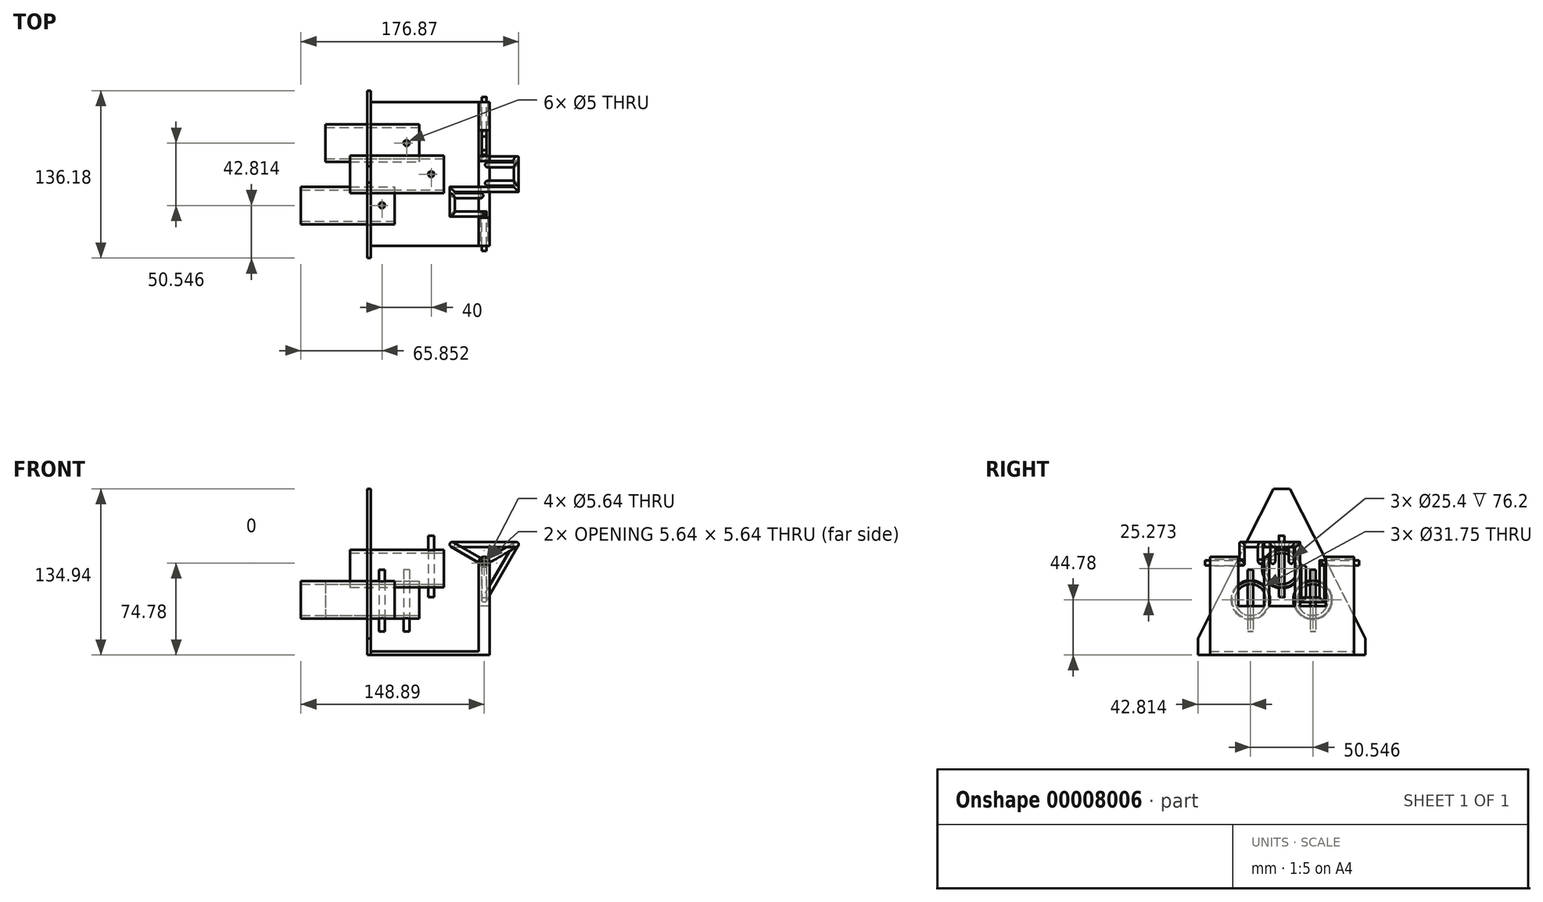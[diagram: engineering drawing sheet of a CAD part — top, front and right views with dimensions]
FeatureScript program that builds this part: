
annotation { "Feature Type Name" : "Feature", "Feature Type Description" : "" }
export const myFeature = defineFeature(function(context is Context, id is Id, definition is map)
    precondition{}
    {
        {
            var Q0;
            Q0=qCreatedBy(makeId("Front.planeOp"),FACE);
            var sketch = newSketch(context, id + "F0", { "sketchPlane" : qUnion([Q0])});
            skCircle(sketch, "E0", {"center": v(0, 0) * mm, "radius": 2 * mm});
            skLineSegment(sketch, "E1", {"start": v(0, 0) * mm, "end": v(-25.98, 15) * mm, "construction": true});
            skLineSegment(sketch, "E2", {"start": v(0, 0) * mm, "end": v(25.98, 15) * mm, "construction": true});
            skLineSegment(sketch, "E3", {"start": v(0, 0) * mm, "end": v(0, -30) * mm, "construction": true});
            skSolve(sketch);
        }
        {
            var Q0;
            Q0=qCreatedBy(makeId("Top.planeOp"),FACE);
            var sketch = newSketch(context, id + "F1", { "sketchPlane" : qUnion([Q0])});
            skLineSegment(sketch, "E4", {"start": v(0, 0) * mm, "end": v(0, 30) * mm});
            skLineSegment(sketch, "E5", {"start": v(0, 45) * mm, "end": v(0, 55) * mm});
            skLineSegment(sketch, "E6", {"start": v(0, 70) * mm, "end": v(0, 80) * mm});
            skLineSegment(sketch, "E7", {"start": v(0, 95) * mm, "end": v(0, 125) * mm});
            skLineSegment(sketch, "E8", {"start": v(0, 30) * mm, "end": v(0, 45) * mm, "construction": true});
            skLineSegment(sketch, "E9", {"start": v(0, 55) * mm, "end": v(0, 70) * mm, "construction": true});
            skLineSegment(sketch, "E10", {"start": v(0, 80) * mm, "end": v(0, 95) * mm, "construction": true});
            skSolve(sketch);
        }
        {
            var Q0;
            Q0=sQuery(id+"F0.wireOp",VERTEX,"E1.end");
            var Q1;
            Q1=sQuery(id+"F0.wireOp",VERTEX,"E2.start");
            var Q2;
            Q2=sQuery(id+"F1.wireOp",VERTEX,"E8.start");
            cPlane(context, id + "F2", {"entities" : qUnion([Q0, Q1, Q2]), "cplaneType" : CPlaneType.THREE_POINT, "offset" : 150 * mm, "width" : 150 * mm, "height" : 150 * mm});
        }
        {
            var Q0;
            Q0=sQuery(id+"F0.wireOp",VERTEX,"E2.end");
            var Q1;
            Q1=sQuery(id+"F0.wireOp",VERTEX,"E2.start");
            var Q2;
            Q2=sQuery(id+"F1.wireOp",VERTEX,"E8.start");
            cPlane(context, id + "F3", {"entities" : qUnion([Q0, Q1, Q2]), "cplaneType" : CPlaneType.THREE_POINT, "offset" : 150 * mm, "width" : 150 * mm, "height" : 150 * mm});
        }
        {
            var Q0;
            Q0=qCreatedBy(id+"F2.planeOp",FACE);
            var sketch = newSketch(context, id + "F4", { "sketchPlane" : qUnion([Q0])});
            skLineSegment(sketch, "E11.0", {"start": v(0, 0) * mm, "end": v(-30, 0) * mm, "construction": true});
            skLineSegment(sketch, "E12.0", {"start": v(0, -30) * mm, "end": v(0, -45) * mm, "construction": true});
            skLineSegment(sketch, "E13", {"start": v(0, -30) * mm, "end": v(-30, -30) * mm});
            skLineSegment(sketch, "E14", {"start": v(-30, -30) * mm, "end": v(-30, -45) * mm});
            skLineSegment(sketch, "E15", {"start": v(-30, -45) * mm, "end": v(0, -45) * mm});
            skSolve(sketch);
        }
        {
            var Q0;
            Q0=qCreatedBy(id+"F3.planeOp",FACE);
            var sketch = newSketch(context, id + "F5", { "sketchPlane" : qUnion([Q0])});
            skLineSegment(sketch, "E16.0", {"start": v(0, 0) * mm, "end": v(30, 0) * mm, "construction": true});
            skLineSegment(sketch, "E16.1", {"start": v(0, 55) * mm, "end": v(0, 70) * mm, "construction": true});
            skLineSegment(sketch, "E17", {"start": v(0, 55) * mm, "end": v(30, 55) * mm});
            skLineSegment(sketch, "E18", {"start": v(30, 55) * mm, "end": v(30, 70) * mm});
            skLineSegment(sketch, "E19", {"start": v(30, 70) * mm, "end": v(0, 70) * mm});
            skSolve(sketch);
        }
        {
            var Q0;
            Q0=qCreatedBy(makeId("Right.planeOp"),FACE);
            var sketch = newSketch(context, id + "F6", { "sketchPlane" : qUnion([Q0])});
            skLineSegment(sketch, "E20.0", {"start": v(0, 0) * mm, "end": v(0, -30) * mm, "construction": true});
            skLineSegment(sketch, "E20.1", {"start": v(80, 0) * mm, "end": v(95, 0) * mm, "construction": true});
            skLineSegment(sketch, "E21", {"start": v(80, 0) * mm, "end": v(80, -30) * mm});
            skLineSegment(sketch, "E22", {"start": v(80, -30) * mm, "end": v(95, -30) * mm});
            skLineSegment(sketch, "E23", {"start": v(95, -30) * mm, "end": v(95, 0) * mm});
            skSolve(sketch);
        }
        {
            var Q0;
            Q0=makeQuery(id+"F0.imprint","IMPRINT",FACE,{"disambiguationData":[TD([[makeQuery(id+"F0.imprint","IMPRINT",EDGE,{"derivedFrom":sQuery(id+"F0.wireOp",EDGE,"E0")}),1.0]])]});
            var Q1;
            Q1=sQuery(id+"F1.wireOp",EDGE,"E4");
            var Q2;
            Q2=sQuery(id+"F4.wireOp",EDGE,"E13");
            var Q3;
            Q3=sQuery(id+"F4.wireOp",EDGE,"E14");
            var Q4;
            Q4=sQuery(id+"F4.wireOp",EDGE,"E15");
            var Q5;
            Q5=sQuery(id+"F1.wireOp",EDGE,"E5");
            var Q6;
            Q6=sQuery(id+"F5.wireOp",EDGE,"E17");
            var Q7;
            Q7=sQuery(id+"F5.wireOp",EDGE,"E19");
            var Q8;
            Q8=sQuery(id+"F5.wireOp",EDGE,"E18");
            var Q9;
            Q9=sQuery(id+"F1.wireOp",EDGE,"E6");
            var Q10;
            Q10=sQuery(id+"F6.wireOp",EDGE,"E21");
            var Q11;
            Q11=sQuery(id+"F6.wireOp",EDGE,"E22");
            var Q12;
            Q12=sQuery(id+"F6.wireOp",EDGE,"E23");
            var Q13;
            Q13=sQuery(id+"F1.wireOp",EDGE,"E7");
            sweep(context, id + "F7", {"profiles" : qUnion([Q0]), "path" : qUnion([Q1, Q2, Q3, Q4, Q5, Q6, Q7, Q8, Q9, Q10, Q11, Q12, Q13])});
        }
        {
            var Q0;
            Q0=qCreatedBy(makeId("Right.planeOp"),FACE);
            var sketch = newSketch(context, id + "F8", { "sketchPlane" : qUnion([Q0])});
            skLineSegment(sketch, "E24", {"start": v(4, -44.64) * mm, "end": v(4, 5) * mm});
            skLineSegment(sketch, "E25", {"start": v(4, 5) * mm, "end": v(27, 5) * mm});
            skLineSegment(sketch, "E26", {"start": v(27, 5) * mm, "end": v(27, -35) * mm});
            skLineSegment(sketch, "E27", {"start": v(27, -35) * mm, "end": v(47.92, -35) * mm});
            skLineSegment(sketch, "E28", {"start": v(47.92, -35) * mm, "end": v(47.92, 5) * mm});
            skLineSegment(sketch, "E29", {"start": v(47.92, 5) * mm, "end": v(52.04, 5) * mm});
            skLineSegment(sketch, "E30", {"start": v(52.04, 5) * mm, "end": v(52.04, -35) * mm});
            skLineSegment(sketch, "E31", {"start": v(52.04, -35) * mm, "end": v(72.96, -35) * mm});
            skLineSegment(sketch, "E32", {"start": v(72.96, -35) * mm, "end": v(72.96, 5) * mm});
            skLineSegment(sketch, "E33", {"start": v(72.96, 5) * mm, "end": v(77.08, 5) * mm});
            skLineSegment(sketch, "E34", {"start": v(77.08, 5) * mm, "end": v(77.08, -35) * mm});
            skLineSegment(sketch, "E35", {"start": v(77.08, -35) * mm, "end": v(98, -35) * mm});
            skLineSegment(sketch, "E36", {"start": v(98, -35) * mm, "end": v(98, 5) * mm});
            skLineSegment(sketch, "E37", {"start": v(98, 5) * mm, "end": v(121, 5) * mm});
            skLineSegment(sketch, "E38", {"start": v(121, 5) * mm, "end": v(121, -44.64) * mm});
            skLineSegment(sketch, "E39", {"start": v(121, -44.64) * mm, "end": v(4, -44.64) * mm});
            skSolve(sketch);
        }
        {
            var Q0;
            Q0=makeQuery(id+"F8.imprint","IMPRINT",FACE,{"disambiguationData":[TD([[makeQuery(id+"F8.imprint","IMPRINT",EDGE,{"derivedFrom":sQuery(id+"F8.wireOp",EDGE,"E24")}),-1.0]])]});
            extrude(context, id + "F9", {"entities" : qUnion([Q0]), "endBound" : BoundingType.SYMMETRIC, "depth" : 9 * mm});
        }
        {
            var Q0;
            Q0=makeQuery(id+"F9.opExtrude","SWEPT_FACE",FACE,{"disambiguationData":[OSD([sQuery(id+"F8.wireOp",EDGE,"E24")])]});
            var sketch = newSketch(context, id + "F10", { "sketchPlane" : qUnion([Q0])});
            skCircle(sketch, "E40", {"center": v(0, 0) * mm, "radius": 2.82 * mm});
            skSolve(sketch);
        }
        {
            var Q0;
            Q0=makeQuery(id+"F9.opExtrude","CAP_FACE",FACE,{"disambiguationData":[OSD([sQuery(id+"F8.wireOp",EDGE,"E24"),sQuery(id+"F8.wireOp",EDGE,"E25"),sQuery(id+"F8.wireOp",EDGE,"E26"),sQuery(id+"F8.wireOp",EDGE,"E27"),sQuery(id+"F8.wireOp",EDGE,"E28"),sQuery(id+"F8.wireOp",EDGE,"E29"),sQuery(id+"F8.wireOp",EDGE,"E30"),sQuery(id+"F8.wireOp",EDGE,"E31"),sQuery(id+"F8.wireOp",EDGE,"E32"),sQuery(id+"F8.wireOp",EDGE,"E33"),sQuery(id+"F8.wireOp",EDGE,"E34"),sQuery(id+"F8.wireOp",EDGE,"E35"),sQuery(id+"F8.wireOp",EDGE,"E36"),sQuery(id+"F8.wireOp",EDGE,"E37"),sQuery(id+"F8.wireOp",EDGE,"E38"),sQuery(id+"F8.wireOp",EDGE,"E39")])],"isStart":false});
            var sketch = newSketch(context, id + "F11", { "sketchPlane" : qUnion([Q0])});
            skLineSegment(sketch, "E41.0.0", {"start": v(4, 5) * mm, "end": v(4, -44.64) * mm});
            skLineSegment(sketch, "E41.0.1", {"start": v(4, -44.64) * mm, "end": v(121, -44.64) * mm});
            skLineSegment(sketch, "E41.0.2", {"start": v(121, -44.64) * mm, "end": v(121, 5) * mm});
            skLineSegment(sketch, "E41.0.3", {"start": v(121, 5) * mm, "end": v(98, 5) * mm});
            skLineSegment(sketch, "E41.0.4", {"start": v(98, 5) * mm, "end": v(98, -35) * mm});
            skLineSegment(sketch, "E41.0.5", {"start": v(98, -35) * mm, "end": v(77.08, -35) * mm});
            skLineSegment(sketch, "E41.0.6", {"start": v(77.08, -35) * mm, "end": v(77.08, 5) * mm});
            skLineSegment(sketch, "E41.0.7", {"start": v(77.08, 5) * mm, "end": v(72.96, 5) * mm});
            skLineSegment(sketch, "E41.0.8", {"start": v(72.96, 5) * mm, "end": v(72.96, -35) * mm});
            skLineSegment(sketch, "E41.0.9", {"start": v(72.96, -35) * mm, "end": v(52.04, -35) * mm});
            skLineSegment(sketch, "E41.0.10", {"start": v(52.04, -35) * mm, "end": v(52.04, 5) * mm});
            skLineSegment(sketch, "E41.0.11", {"start": v(52.04, 5) * mm, "end": v(47.92, 5) * mm});
            skLineSegment(sketch, "E41.0.12", {"start": v(47.92, 5) * mm, "end": v(47.92, -35) * mm});
            skLineSegment(sketch, "E41.0.13", {"start": v(47.92, -35) * mm, "end": v(27, -35) * mm});
            skLineSegment(sketch, "E41.0.14", {"start": v(27, -35) * mm, "end": v(27, 5) * mm});
            skLineSegment(sketch, "E41.0.15", {"start": v(27, 5) * mm, "end": v(4, 5) * mm});
            skLineSegment(sketch, "E42", {"start": v(47.92, -35) * mm, "end": v(52.04, -35) * mm});
            skLineSegment(sketch, "E43", {"start": v(72.96, -35) * mm, "end": v(77.08, -35) * mm});
            skSolve(sketch);
        }
        {
            var Q0;
            Q0=makeQuery(id+"F11.imprint","IMPRINT",FACE,{"disambiguationData":[TD([[makeQuery(id+"F11.imprint","IMPRINT",EDGE,{"derivedFrom":sQuery(id+"F11.wireOp",EDGE,"E41.0.0")}),-1.0]])]});
            extrude(context, id + "F12", {"entities" : qUnion([Q0]), "oppositeDirection" : true, "depth" : 9 * mm});
        }
        {
            var Q0;
            Q0=makeQuery(id+"F10.imprint","IMPRINT",FACE,{"disambiguationData":[TD([[makeQuery(id+"F10.imprint","IMPRINT",EDGE,{"derivedFrom":sQuery(id+"F10.wireOp",EDGE,"E40")}),1.0]])]});
            extrude(context, id + "F13", {"entities" : qUnion([Q0]), "operationType" : NewBodyOperationType.REMOVE, "endBound" : BoundingType.THROUGH_ALL, "oppositeDirection" : true, "depth" : 25 * mm});
        }
        {
            var Q0;
            Q0=makeQuery(id+"F9.opExtrude","CAP_EDGE",EDGE,{"disambiguationData":[OSD([sQuery(id+"F8.wireOp",EDGE,"E25")])],"isStart":true});
            var Q1;
            Q1=makeQuery(id+"F9.opExtrude","CAP_EDGE",EDGE,{"disambiguationData":[OSD([sQuery(id+"F8.wireOp",EDGE,"E29")])],"isStart":false});
            var Q2;
            Q2=makeQuery(id+"F9.opExtrude","CAP_EDGE",EDGE,{"disambiguationData":[OSD([sQuery(id+"F8.wireOp",EDGE,"E29")])],"isStart":true});
            var Q3;
            Q3=makeQuery(id+"F9.opExtrude","CAP_EDGE",EDGE,{"disambiguationData":[OSD([sQuery(id+"F8.wireOp",EDGE,"E33")])],"isStart":false});
            var Q4;
            Q4=makeQuery(id+"F9.opExtrude","CAP_EDGE",EDGE,{"disambiguationData":[OSD([sQuery(id+"F8.wireOp",EDGE,"E33")])],"isStart":true});
            var Q5;
            Q5=makeQuery(id+"F9.opExtrude","CAP_EDGE",EDGE,{"disambiguationData":[OSD([sQuery(id+"F8.wireOp",EDGE,"E37")])],"isStart":false});
            var Q6;
            Q6=makeQuery(id+"F9.opExtrude","CAP_EDGE",EDGE,{"disambiguationData":[OSD([sQuery(id+"F8.wireOp",EDGE,"E37")])],"isStart":true});
            var Q7;
            Q7=makeQuery(id+"F9.opExtrude","CAP_EDGE",EDGE,{"disambiguationData":[OSD([sQuery(id+"F8.wireOp",EDGE,"E25")])],"isStart":false});
            var Q8;
            Q8=makeQuery(id+"F12.opExtrude","CAP_EDGE",EDGE,{"disambiguationData":[OSD([sQuery(id+"F11.wireOp",EDGE,"E41.0.15")])],"isStart":true});
            var Q9;
            Q9=makeQuery(id+"F12.opExtrude","CAP_EDGE",EDGE,{"disambiguationData":[OSD([sQuery(id+"F11.wireOp",EDGE,"E41.0.15")])],"isStart":false});
            var Q10;
            Q10=makeQuery(id+"F12.opExtrude","CAP_EDGE",EDGE,{"disambiguationData":[OSD([sQuery(id+"F11.wireOp",EDGE,"E41.0.3")])],"isStart":true});
            var Q11;
            Q11=makeQuery(id+"F12.opExtrude","CAP_EDGE",EDGE,{"disambiguationData":[OSD([sQuery(id+"F11.wireOp",EDGE,"E41.0.3")])],"isStart":false});
            fillet(context, id + "F14", {"entities" : qUnion([Q0, Q1, Q2, Q3, Q4, Q5, Q6, Q7, Q8, Q9, Q10, Q11]), "radius" : 4.5 * mm, "tangentPropagation" : true, "allowEdgeOverflow" : false});
        }
        {
            var Q0;
            Q0=qCreatedBy(id+"F2.planeOp",FACE);
            var sketch = newSketch(context, id + "F15", { "sketchPlane" : qUnion([Q0])});
            skLineSegment(sketch, "E44.0", {"start": v(0, -45) * mm, "end": v(0, -55) * mm, "construction": true});
            skLineSegment(sketch, "E44.1", {"start": v(0, 0) * mm, "end": v(-30, 0) * mm, "construction": true});
            skLineSegment(sketch, "E45.0", {"start": v(0, -30) * mm, "end": v(0, -45) * mm, "construction": true});
            skLineSegment(sketch, "E46", {"start": v(0, -30) * mm, "end": v(-30, -30) * mm});
            skLineSegment(sketch, "E47", {"start": v(0, -50) * mm, "end": v(-30, -50) * mm, "construction": true});
            skLineSegment(sketch, "E48", {"start": v(-30, -50) * mm, "end": v(-30, -30) * mm});
            skSolve(sketch);
        }
        {
            var Q0;
            Q0=qCreatedBy(id+"F3.planeOp",FACE);
            var sketch = newSketch(context, id + "F16", { "sketchPlane" : qUnion([Q0])});
            skLineSegment(sketch, "E49.0", {"start": v(0, 0) * mm, "end": v(30, 0) * mm, "construction": true});
            skPoint(sketch, "E49.1", {"position": v(0, 50) * mm});
            skLineSegment(sketch, "E49.2", {"start": v(0, 70) * mm, "end": v(0, 80) * mm, "construction": true});
            skLineSegment(sketch, "E50", {"start": v(0, 75) * mm, "end": v(30, 75) * mm, "construction": true});
            skLineSegment(sketch, "E51", {"start": v(30, 75) * mm, "end": v(30, 50) * mm});
            skSolve(sketch);
        }
        {
            var Q0;
            Q0=sQuery(id+"F16.wireOp",VERTEX,"E50.end");
            var Q1;
            Q1=sQuery(id+"F16.wireOp",VERTEX,"E51.end");
            var Q2;
            Q2=sQuery(id+"F15.wireOp",VERTEX,"E47.end");
            cPlane(context, id + "F17", {"entities" : qUnion([Q0, Q1, Q2]), "cplaneType" : CPlaneType.THREE_POINT, "offset" : 150 * mm, "width" : 150 * mm, "height" : 150 * mm});
        }
        {
            var Q0;
            Q0=qCreatedBy(id+"F17.planeOp",FACE);
            var sketch = newSketch(context, id + "F18", { "sketchPlane" : qUnion([Q0])});
            skPoint(sketch, "E52.0", {"position": v(25.98, 50) * mm});
            skPoint(sketch, "E52.1", {"position": v(-25.98, 50) * mm});
            skLineSegment(sketch, "E53", {"start": v(-25.98, 50) * mm, "end": v(25.98, 50) * mm});
            skSolve(sketch);
        }
        {
            var Q0;
            Q0=sQuery(id+"F6.wireOp",VERTEX,"E22.end");
            var Q1;
            Q1=sQuery(id+"F6.wireOp",VERTEX,"E22.start");
            var Q2;
            Q2=sQuery(id+"F16.wireOp",VERTEX,"E51.start");
            cPlane(context, id + "F19", {"entities" : qUnion([Q0, Q1, Q2]), "cplaneType" : CPlaneType.THREE_POINT, "offset" : 150 * mm, "width" : 150 * mm, "height" : 150 * mm});
        }
        {
            var Q0;
            Q0=qCreatedBy(id+"F19.planeOp",FACE);
            var sketch = newSketch(context, id + "F20", { "sketchPlane" : qUnion([Q0])});
            skPoint(sketch, "E54.0", {"position": v(95, -25.98) * mm});
            skPoint(sketch, "E54.1", {"position": v(75, 25.98) * mm});
            skLineSegment(sketch, "E55", {"start": v(75, 25.98) * mm, "end": v(75, -25.98) * mm});
            skLineSegment(sketch, "E56", {"start": v(75, -25.98) * mm, "end": v(95, -25.98) * mm});
            skSolve(sketch);
        }
        {
            var Q0;
            Q0=makeQuery(id+"F0.imprint","IMPRINT",FACE,{"disambiguationData":[TD([[makeQuery(id+"F0.imprint","IMPRINT",EDGE,{"derivedFrom":sQuery(id+"F0.wireOp",EDGE,"E0")}),1.0]])]});
            var Q1;
            Q1=sQuery(id+"F1.wireOp",EDGE,"E4");
            var Q2;
            Q2=sQuery(id+"F15.wireOp",EDGE,"E46");
            var Q3;
            Q3=sQuery(id+"F15.wireOp",EDGE,"E48");
            var Q4;
            Q4=sQuery(id+"F18.wireOp",EDGE,"E53");
            var Q5;
            Q5=sQuery(id+"F16.wireOp",EDGE,"E51");
            var Q6;
            Q6=sQuery(id+"F20.wireOp",EDGE,"E55");
            var Q7;
            Q7=sQuery(id+"F20.wireOp",EDGE,"E56");
            var Q8;
            Q8=sQuery(id+"F6.wireOp",EDGE,"E23");
            var Q9;
            Q9=sQuery(id+"F1.wireOp",EDGE,"E7");
            sweep(context, id + "F21", {"profiles" : qUnion([Q0]), "path" : qUnion([Q1, Q2, Q3, Q4, Q5, Q6, Q7, Q8, Q9])});
        }
        {
            var Q0;
            Q0=makeQuery(id+"F12.opExtrude","CAP_FACE",FACE,{"disambiguationData":[OSD([sQuery(id+"F11.wireOp",EDGE,"E41.0.0"),sQuery(id+"F11.wireOp",EDGE,"E41.0.1"),sQuery(id+"F11.wireOp",EDGE,"E41.0.2"),sQuery(id+"F11.wireOp",EDGE,"E41.0.3"),sQuery(id+"F11.wireOp",EDGE,"E41.0.4"),sQuery(id+"F11.wireOp",EDGE,"E41.0.5"),sQuery(id+"F11.wireOp",EDGE,"E41.0.9"),sQuery(id+"F11.wireOp",EDGE,"E41.0.13"),sQuery(id+"F11.wireOp",EDGE,"E41.0.14"),sQuery(id+"F11.wireOp",EDGE,"E41.0.15"),sQuery(id+"F11.wireOp",EDGE,"E42"),sQuery(id+"F11.wireOp",EDGE,"E43")])],"isStart":false});
            var sketch = newSketch(context, id + "F22", { "sketchPlane" : qUnion([Q0])});
            skCircle(sketch, "E57", {"center": v(-87.5, -30) * mm, "radius": 15.24 * mm});
            skCircle(sketch, "E58", {"center": v(-36.95, -30) * mm, "radius": 15.24 * mm});
            skCircle(sketch, "E59", {"center": v(-62.23, -4.73) * mm, "radius": 15.24 * mm});
            skLineSegment(sketch, "E60", {"start": v(-62.23, -30) * mm, "end": v(-62.23, -4.73) * mm, "construction": true});
            skLineSegment(sketch, "E61", {"start": v(-87.5, -30) * mm, "end": v(-62.23, -30) * mm, "construction": true});
            skLineSegment(sketch, "E62", {"start": v(-62.23, -30) * mm, "end": v(-36.95, -30) * mm, "construction": true});
            skCircle(sketch, "E63", {"center": v(-87.5, -30) * mm, "radius": 12.7 * mm});
            skCircle(sketch, "E64", {"center": v(-62.23, -4.73) * mm, "radius": 12.7 * mm});
            skCircle(sketch, "E65", {"center": v(-36.95, -30) * mm, "radius": 12.7 * mm});
            skSolve(sketch);
        }
        {
            var Q0;
            {var subQ3=sQuery(id+"F22.wireOp",EDGE,"E57");var subQ5=makeQuery(id+"F12.opExtrude","CAP_EDGE",EDGE,{"disambiguationData":[OSD([sQuery(id+"F11.wireOp",EDGE,"E41.0.4")])],"isStart":false});var subQ7=makeQuery(id+"F22.imprint","INTERSECT",VERTEX,{"derivedFrom":[subQ5,subQ3]});Q0=makeQuery(id+"F22.imprint","IMPRINT",FACE,{"disambiguationData":[TD([[makeQuery(id+"F22.imprint","IMPRINT",EDGE,{"disambiguationData":[TD([[subQ7,1.0]])],"derivedFrom":subQ5}),-1.0]])]});}
            var Q1;
            {var subQ3=sQuery(id+"F22.wireOp",EDGE,"E57");var subQ5=makeQuery(id+"F12.opExtrude","CAP_EDGE",EDGE,{"disambiguationData":[OSD([sQuery(id+"F11.wireOp",EDGE,"E41.0.1")])],"isStart":false});var subQ7=makeQuery(id+"F22.imprint","INTERSECT",VERTEX,{"disambiguationData":[OD(0.0)],"derivedFrom":[subQ5,subQ3]});Q1=makeQuery(id+"F22.imprint","IMPRINT",FACE,{"disambiguationData":[TD([[makeQuery(id+"F22.imprint","IMPRINT",EDGE,{"disambiguationData":[TD([[subQ7,1.0]])],"derivedFrom":subQ3}),1.0]])]});}
            var Q2;
            Q2=makeQuery(id+"F22.imprint","IMPRINT",FACE,{"disambiguationData":[TD([[makeQuery(id+"F22.imprint","IMPRINT",EDGE,{"derivedFrom":sQuery(id+"F22.wireOp",EDGE,"E59")}),1.0]])]});
            var Q3;
            {var subQ3=sQuery(id+"F22.wireOp",EDGE,"E58");var subQ5=makeQuery(id+"F12.opExtrude","CAP_EDGE",EDGE,{"disambiguationData":[OSD([sQuery(id+"F11.wireOp",EDGE,"E41.0.14")])],"isStart":false});var subQ7=makeQuery(id+"F22.imprint","INTERSECT",VERTEX,{"derivedFrom":[subQ5,subQ3]});Q3=makeQuery(id+"F22.imprint","IMPRINT",FACE,{"disambiguationData":[TD([[makeQuery(id+"F22.imprint","IMPRINT",EDGE,{"disambiguationData":[TD([[subQ7,-1.0]])],"derivedFrom":subQ5}),-1.0]])]});}
            var Q4;
            {var subQ3=sQuery(id+"F22.wireOp",EDGE,"E58");var subQ8=makeQuery(id+"F12.opExtrude","CAP_EDGE",EDGE,{"disambiguationData":[OSD([sQuery(id+"F11.wireOp",EDGE,"E41.0.14")])],"isStart":false});var subQ10=makeQuery(id+"F22.imprint","INTERSECT",VERTEX,{"derivedFrom":[subQ8,subQ3]});Q4=makeQuery(id+"F22.imprint","IMPRINT",FACE,{"disambiguationData":[TD([[makeQuery(id+"F22.imprint","IMPRINT",EDGE,{"disambiguationData":[TD([[subQ10,1.0]])],"derivedFrom":subQ3}),1.0]])]});}
            var Q5;
            {var subQ0=makeQuery(id+"F12.opExtrude","CAP_EDGE",EDGE,{"disambiguationData":[OSD([sQuery(id+"F11.wireOp",EDGE,"E41.0.1")])],"isStart":false});var subQ1=sQuery(id+"F22.wireOp",EDGE,"E57");var subQ3=makeQuery(id+"F22.imprint","INTERSECT",VERTEX,{"disambiguationData":[OD(0.0)],"derivedFrom":[subQ0,subQ1]});Q5=makeQuery(id+"F22.imprint","IMPRINT",FACE,{"disambiguationData":[TD([[makeQuery(id+"F22.imprint","IMPRINT",EDGE,{"disambiguationData":[TD([[subQ3,-1.0]])],"derivedFrom":subQ1}),1.0]])]});}
            var Q6;
            {var subQ0=makeQuery(id+"F12.opExtrude","CAP_EDGE",EDGE,{"disambiguationData":[OSD([sQuery(id+"F11.wireOp",EDGE,"E41.0.1")])],"isStart":false});var subQ1=sQuery(id+"F22.wireOp",EDGE,"E58");var subQ3=makeQuery(id+"F22.imprint","INTERSECT",VERTEX,{"disambiguationData":[OD(0.0)],"derivedFrom":[subQ0,subQ1]});Q6=makeQuery(id+"F22.imprint","IMPRINT",FACE,{"disambiguationData":[TD([[makeQuery(id+"F22.imprint","IMPRINT",EDGE,{"disambiguationData":[TD([[subQ3,-1.0]])],"derivedFrom":subQ1}),1.0]])]});}
            extrude(context, id + "F23", {"entities" : qUnion([Q0, Q1, Q2, Q3, Q4, Q5, Q6]), "depth" : 76.2 * mm});
        }
        {
            var Q0;
            Q0=makeQuery(id+"F23.opExtrude","SWEPT_BODY",BODY,{"disambiguationData":[OSD([sQuery(id+"F22.wireOp",EDGE,"E59"),sQuery(id+"F22.wireOp",EDGE,"E64")])]});
            var Q1;
            Q1=makeQuery(id+"F23.opExtrude","SWEPT_BODY",BODY,{"disambiguationData":[OSD([sQuery(id+"F11.wireOp",EDGE,"E41.0.1"),sQuery(id+"F22.wireOp",EDGE,"E57"),sQuery(id+"F22.wireOp",EDGE,"E63")])]});
            var Q2;
            Q2=makeQuery(id+"F23.opExtrude","SWEPT_BODY",BODY,{"disambiguationData":[OSD([sQuery(id+"F11.wireOp",EDGE,"E41.0.1"),sQuery(id+"F22.wireOp",EDGE,"E58"),sQuery(id+"F22.wireOp",EDGE,"E65")])]});
            transform(context, id + "F24", {"entities" : qUnion([Q0, Q1, Q2]), "transformType" : TransformType.TRANSLATION_3D, "dx" : -48.19 * mm, "dy" : 0 * mm, "dz" : 0 * mm, "makeCopy" : false});
        }
        {
            var Q0;
            Q0=makeQuery(id+"F9.opExtrude","SWEPT_FACE",FACE,{"disambiguationData":[OSD([sQuery(id+"F8.wireOp",EDGE,"E31")])]});
            var sketch = newSketch(context, id + "F25", { "sketchPlane" : qUnion([Q0])});
            skCircle(sketch, "E66", {"center": v(-63.04, 87.5) * mm, "radius": 2.5 * mm});
            skCircle(sketch, "E67", {"center": v(-63.04, 62.23) * mm, "radius": 2.5 * mm});
            skCircle(sketch, "E68", {"center": v(-63.04, 36.95) * mm, "radius": 2.5 * mm});
            skLineSegment(sketch, "E69", {"start": v(-63.04, 87.5) * mm, "end": v(-63.04, 62.23) * mm, "construction": true});
            skLineSegment(sketch, "E70", {"start": v(-63.04, 62.23) * mm, "end": v(-63.04, 36.95) * mm, "construction": true});
            skLineSegment(sketch, "E71", {"start": v(-128.81, 36.95) * mm, "end": v(-63.04, 36.95) * mm, "construction": true});
            skLineSegment(sketch, "E72.0", {"start": v(-128.89, 46.99) * mm, "end": v(-128.89, 77.47) * mm});
            skLineSegment(sketch, "E73", {"start": v(-128.89, 62.23) * mm, "end": v(-63.04, 62.23) * mm, "construction": true});
            skLineSegment(sketch, "E74.0", {"start": v(-128.89, 72.26) * mm, "end": v(-128.89, 102.74) * mm});
            skLineSegment(sketch, "E75", {"start": v(-128.89, 87.5) * mm, "end": v(-63.04, 87.5) * mm, "construction": true});
            skSolve(sketch);
        }
        {
            var Q0;
            Q0=makeQuery(id+"F25.imprint","IMPRINT",FACE,{"disambiguationData":[TD([[makeQuery(id+"F25.imprint","IMPRINT",EDGE,{"derivedFrom":sQuery(id+"F25.wireOp",EDGE,"E66")}),1.0]])]});
            var Q1;
            Q1=makeQuery(id+"F25.imprint","IMPRINT",FACE,{"disambiguationData":[TD([[makeQuery(id+"F25.imprint","IMPRINT",EDGE,{"derivedFrom":sQuery(id+"F25.wireOp",EDGE,"E67")}),1.0]])]});
            var Q2;
            Q2=makeQuery(id+"F25.imprint","IMPRINT",FACE,{"disambiguationData":[TD([[makeQuery(id+"F25.imprint","IMPRINT",EDGE,{"derivedFrom":sQuery(id+"F25.wireOp",EDGE,"E68")}),1.0]])]});
            var Q3;
            Q3=sQuery(id+"F25.wireOp",EDGE,"E66");
            var Q4;
            Q4=makeQuery(id+"F23.opExtrude","SWEPT_FACE",FACE,{"disambiguationData":[OSD([sQuery(id+"F22.wireOp",EDGE,"E57")])]});
            extrude(context, id + "F26", {"entities" : qUnion([Q0, Q1, Q2]), "operationType" : NewBodyOperationType.REMOVE, "surfaceEntities" : qUnion([Q3]), "endBound" : BoundingType.SYMMETRIC, "endBoundEntity" : qUnion([Q4]), "depth" : 100.72 * mm});
        }
        {
            var Q0;
            Q0=makeQuery(id+"F23.opExtrude","SWEPT_BODY",BODY,{"disambiguationData":[OSD([sQuery(id+"F22.wireOp",EDGE,"E58"),sQuery(id+"F22.wireOp",EDGE,"E65")])]});
            transform(context, id + "F27", {"entities" : qUnion([Q0]), "transformType" : TransformType.TRANSLATION_3D, "dx" : -20 * mm, "dy" : 0 * mm, "dz" : 0 * mm, "makeCopy" : false});
        }
        {
            var Q0;
            Q0=makeQuery(id+"F23.opExtrude","SWEPT_BODY",BODY,{"disambiguationData":[OSD([sQuery(id+"F22.wireOp",EDGE,"E59"),sQuery(id+"F22.wireOp",EDGE,"E64")])]});
            transform(context, id + "F28", {"entities" : qUnion([Q0]), "transformType" : TransformType.TRANSLATION_3D, "dx" : 20 * mm, "dy" : 0 * mm, "dz" : 0 * mm, "makeCopy" : false});
        }
        {
            var Q0;
            Q0=makeQuery(id+"F9.opExtrude","SWEPT_FACE",FACE,{"disambiguationData":[OSD([sQuery(id+"F8.wireOp",EDGE,"E31")])]});
            var sketch = newSketch(context, id + "F29", { "sketchPlane" : qUnion([Q0])});
            skCircle(sketch, "E76", {"center": v(-63.04, 87.5) * mm, "radius": 2.25 * mm});
            skCircle(sketch, "E77", {"center": v(-43.04, 62.23) * mm, "radius": 2.25 * mm});
            skCircle(sketch, "E78", {"center": v(-83.04, 36.95) * mm, "radius": 2.25 * mm});
            skCircle(sketch, "E79.0", {"center": v(-63.04, 87.5) * mm, "radius": 2.5 * mm, "construction": true});
            skCircle(sketch, "E79.1", {"center": v(-43.04, 62.23) * mm, "radius": 2.5 * mm, "construction": true});
            skCircle(sketch, "E79.2", {"center": v(-83.04, 36.95) * mm, "radius": 2.5 * mm, "construction": true});
            skSolve(sketch);
        }
        {
            var Q0;
            Q0 = qSketchRegion(id + "F29", true);
            extrude(context, id + "F30", {"entities" : qUnion([Q0]), "endBound" : BoundingType.SYMMETRIC, "depth" : 50 * mm});
        }
        {
            var Q0;
            Q0=makeQuery(id+"F30.opExtrude","SWEPT_BODY",BODY,{"disambiguationData":[OSD([sQuery(id+"F29.wireOp",EDGE,"E78"),sQuery(id+"F29.wireOp",EDGE,"E79.2")])]});
            var Q1;
            Q1=makeQuery(id+"F30.opExtrude","SWEPT_BODY",BODY,{"disambiguationData":[OSD([sQuery(id+"F29.wireOp",EDGE,"E76"),sQuery(id+"F29.wireOp",EDGE,"E79.0")])]});
            var Q2;
            Q2=makeQuery(id+"F30.opExtrude","SWEPT_BODY",BODY,{"disambiguationData":[OSD([sQuery(id+"F29.wireOp",EDGE,"E77"),sQuery(id+"F29.wireOp",EDGE,"E79.1")])]});
            transform(context, id + "F31", {"entities" : qUnion([Q0, Q1, Q2]), "transformType" : TransformType.TRANSLATION_3D, "dx" : 0 * mm, "dy" : 0 * mm, "dz" : 4.37 * mm, "makeCopy" : false});
        }
        {
            var Q0;
            Q0=makeQuery(id+"F30.opExtrude","SWEPT_BODY",BODY,{"disambiguationData":[OSD([sQuery(id+"F29.wireOp",EDGE,"E77"),sQuery(id+"F29.wireOp",EDGE,"E79.1")])]});
            transform(context, id + "F32", {"entities" : qUnion([Q0]), "transformType" : TransformType.TRANSLATION_3D, "dx" : 0 * mm, "dy" : 0 * mm, "dz" : 27.83 * mm, "makeCopy" : false});
        }
        {
            var Q0;
            Q0=makeQuery(id+"F23.opExtrude","CAP_FACE",FACE,{"disambiguationData":[OSD([sQuery(id+"F22.wireOp",EDGE,"E57"),sQuery(id+"F22.wireOp",EDGE,"E63")])],"isStart":false});
            var sketch = newSketch(context, id + "F33", { "sketchPlane" : qUnion([Q0])});
            skLineSegment(sketch, "E80", {"start": v(-130.32, -61.4) * mm, "end": v(-68.94, 60.16) * mm});
            skLineSegment(sketch, "E81", {"start": v(-68.94, 60.16) * mm, "end": v(-55.52, 60.16) * mm});
            skLineSegment(sketch, "E82", {"start": v(-55.52, 60.16) * mm, "end": v(5.86, -61.4) * mm});
            skLineSegment(sketch, "E83", {"start": v(5.86, -61.4) * mm, "end": v(5.86, -74.82) * mm});
            skLineSegment(sketch, "E84", {"start": v(5.86, -74.82) * mm, "end": v(-130.32, -74.82) * mm});
            skLineSegment(sketch, "E85", {"start": v(-130.32, -61.4) * mm, "end": v(-130.32, -74.82) * mm});
            skCircle(sketch, "E86.0", {"center": v(-87.5, -30) * mm, "radius": 12.7 * mm, "construction": true});
            skCircle(sketch, "E86.1", {"center": v(-62.23, -4.73) * mm, "radius": 12.7 * mm, "construction": true});
            skCircle(sketch, "E86.2", {"center": v(-36.95, -30) * mm, "radius": 12.7 * mm, "construction": true});
            skLineSegment(sketch, "E87", {"start": v(-87.5, -30) * mm, "end": v(-62.23, -30) * mm, "construction": true});
            skLineSegment(sketch, "E88", {"start": v(-36.95, -30) * mm, "end": v(-62.23, -30) * mm, "construction": true});
            skLineSegment(sketch, "E89", {"start": v(-62.23, -30) * mm, "end": v(-62.23, -74.82) * mm, "construction": true});
            skCircle(sketch, "E90", {"center": v(-87.5, -30) * mm, "radius": 15.88 * mm});
            skCircle(sketch, "E91", {"center": v(-62.23, -4.73) * mm, "radius": 15.88 * mm});
            skCircle(sketch, "E92", {"center": v(-36.95, -30) * mm, "radius": 15.88 * mm});
            skSolve(sketch);
        }
        {
            var Q0;
            Q0 = qSketchRegion(id + "F33", true);
            extrude(context, id + "F34", {"entities" : qUnion([Q0]), "depth" : 3 * mm});
        }
        {
            var Q0;
            Q0=makeQuery(id+"F34.opExtrude","SWEPT_BODY",BODY,{"disambiguationData":[OSD([sQuery(id+"F33.wireOp",EDGE,"E80"),sQuery(id+"F33.wireOp",EDGE,"E81"),sQuery(id+"F33.wireOp",EDGE,"E82"),sQuery(id+"F33.wireOp",EDGE,"E83"),sQuery(id+"F33.wireOp",EDGE,"E84"),sQuery(id+"F33.wireOp",EDGE,"E85"),sQuery(id+"F33.wireOp",EDGE,"E90"),sQuery(id+"F33.wireOp",EDGE,"E91"),sQuery(id+"F33.wireOp",EDGE,"E92")])]});
            transform(context, id + "F35", {"entities" : qUnion([Q0]), "transformType" : TransformType.TRANSLATION_3D, "dx" : 36.84 * mm, "dy" : 0 * mm, "dz" : 0 * mm, "makeCopy" : false});
        }
        {
            var Q0;
            Q0=makeQuery(id+"F9.opExtrude","SWEPT_FACE",FACE,{"disambiguationData":[OSD([sQuery(id+"F8.wireOp",EDGE,"E39")])]});
            var Q1;
            Q1=makeQuery(id+"F34.opExtrude","SWEPT_BODY",BODY,{"disambiguationData":[OSD([sQuery(id+"F33.wireOp",EDGE,"E80"),sQuery(id+"F33.wireOp",EDGE,"E81"),sQuery(id+"F33.wireOp",EDGE,"E82"),sQuery(id+"F33.wireOp",EDGE,"E83"),sQuery(id+"F33.wireOp",EDGE,"E84"),sQuery(id+"F33.wireOp",EDGE,"E85"),sQuery(id+"F33.wireOp",EDGE,"E90"),sQuery(id+"F33.wireOp",EDGE,"E91"),sQuery(id+"F33.wireOp",EDGE,"E92")])]});
            extrude(context, id + "F36", {"entities" : qUnion([Q0]), "operationType" : NewBodyOperationType.ADD, "endBoundEntity" : qUnion([Q1]), "depth" : 30.15 * mm});
        }
        {
            var Q0;
            {var subQ0=sQuery(id+"F8.wireOp",EDGE,"E39");Q0=makeQuery(id+"F36.boolean.opBoolean","MERGE",FACE,{"derivedFrom":[makeQuery(id+"F9.opExtrude","CAP_FACE",FACE,{"disambiguationData":[OSD([sQuery(id+"F8.wireOp",EDGE,"E24"),sQuery(id+"F8.wireOp",EDGE,"E25"),sQuery(id+"F8.wireOp",EDGE,"E26"),sQuery(id+"F8.wireOp",EDGE,"E27"),sQuery(id+"F8.wireOp",EDGE,"E28"),sQuery(id+"F8.wireOp",EDGE,"E29"),sQuery(id+"F8.wireOp",EDGE,"E30"),sQuery(id+"F8.wireOp",EDGE,"E31"),sQuery(id+"F8.wireOp",EDGE,"E32"),sQuery(id+"F8.wireOp",EDGE,"E33"),sQuery(id+"F8.wireOp",EDGE,"E34"),sQuery(id+"F8.wireOp",EDGE,"E35"),sQuery(id+"F8.wireOp",EDGE,"E36"),sQuery(id+"F8.wireOp",EDGE,"E37"),sQuery(id+"F8.wireOp",EDGE,"E38"),subQ0])],"isStart":false}),makeQuery(id+"F36.opExtrude","SWEPT_FACE",FACE,{"disambiguationData":[OSD([subQ0]),TDD([makeQuery(id+"F9.opExtrude","CAP_EDGE",EDGE,{"disambiguationData":[OSD([subQ0])],"isStart":false})])]})]});}
            var sketch = newSketch(context, id + "F37", { "sketchPlane" : qUnion([Q0])});
            skLineSegment(sketch, "E93.bottom", {"start": v(4, -74.78) * mm, "end": v(121, -74.78) * mm});
            skLineSegment(sketch, "E93.top", {"start": v(4, -71.78) * mm, "end": v(121, -71.78) * mm});
            skLineSegment(sketch, "E93.left", {"start": v(4, -74.78) * mm, "end": v(4, -71.78) * mm});
            skLineSegment(sketch, "E93.right", {"start": v(121, -74.78) * mm, "end": v(121, -71.78) * mm});
            skSolve(sketch);
        }
        {
            var Q0;
            Q0 = qSketchRegion(id + "F37", true);
            var Q1;
            Q1=makeQuery(id+"F34.opExtrude","SWEPT_BODY",BODY,{"disambiguationData":[OSD([sQuery(id+"F33.wireOp",EDGE,"E80"),sQuery(id+"F33.wireOp",EDGE,"E81"),sQuery(id+"F33.wireOp",EDGE,"E82"),sQuery(id+"F33.wireOp",EDGE,"E83"),sQuery(id+"F33.wireOp",EDGE,"E84"),sQuery(id+"F33.wireOp",EDGE,"E85"),sQuery(id+"F33.wireOp",EDGE,"E90"),sQuery(id+"F33.wireOp",EDGE,"E91"),sQuery(id+"F33.wireOp",EDGE,"E92")])]});
            extrude(context, id + "F38", {"entities" : qUnion([Q0]), "operationType" : NewBodyOperationType.ADD, "endBound" : BoundingType.UP_TO_BODY, "oppositeDirection" : true, "endBoundEntityBody" : qUnion([Q1]), "depth" : 25 * mm});
        }
        {
            var Q0;
            Q0=makeQuery(id+"F34.opExtrude","SWEPT_FACE",FACE,{"disambiguationData":[OSD([sQuery(id+"F33.wireOp",EDGE,"E84")])]});
            var Q1;
            Q1=makeQuery(id+"F38.boolean.opBoolean","MERGE",FACE,{"derivedFrom":[makeQuery(id+"F36.opExtrude","CAP_FACE",FACE,{"disambiguationData":[OSD([sQuery(id+"F8.wireOp",EDGE,"E39")])],"isStart":false}),makeQuery(id+"F38.opExtrude","SWEPT_FACE",FACE,{"disambiguationData":[OSD([sQuery(id+"F37.wireOp",EDGE,"E93.bottom")])]})]});
            extrude(context, id + "F39", {"entities" : qUnion([Q0]), "operationType" : NewBodyOperationType.REMOVE, "endBound" : BoundingType.UP_TO_SURFACE, "oppositeDirection" : true, "endBoundEntityFace" : qUnion([Q1]), "depth" : 25 * mm});
        }
    });
